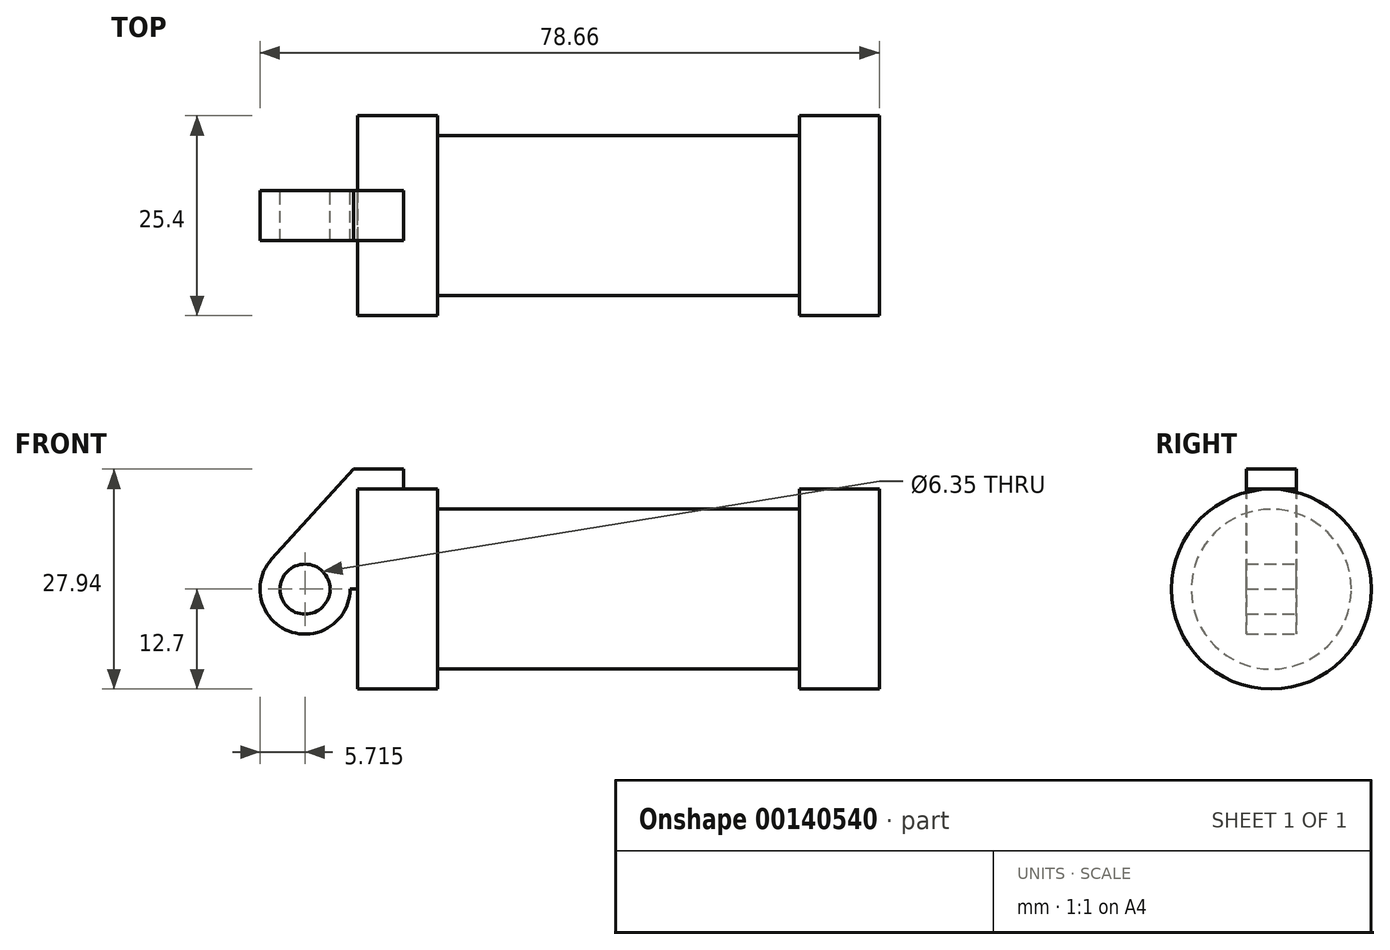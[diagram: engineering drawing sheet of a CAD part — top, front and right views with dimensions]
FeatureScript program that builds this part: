
annotation { "Feature Type Name" : "Feature", "Feature Type Description" : "" }
export const myFeature = defineFeature(function(context is Context, id is Id, definition is map)
    precondition{}
    {
        {
            var Q0;
            Q0=qCreatedBy(makeId("Front.planeOp"),FACE);
            var sketch = newSketch(context, id + "F0", { "sketchPlane" : qUnion([Q0])});
            skLineSegment(sketch, "E0", {"start": v(0, 0) * mm, "end": v(0, 12.7) * mm});
            skLineSegment(sketch, "E1", {"start": v(0, 12.7) * mm, "end": v(10.16, 12.7) * mm});
            skLineSegment(sketch, "E2", {"start": v(10.16, 12.7) * mm, "end": v(10.16, 10.16) * mm});
            skLineSegment(sketch, "E3", {"start": v(10.16, 10.16) * mm, "end": v(56.13, 10.16) * mm});
            skLineSegment(sketch, "E4", {"start": v(56.13, 10.16) * mm, "end": v(56.13, 12.7) * mm});
            skLineSegment(sketch, "E5", {"start": v(56.13, 12.7) * mm, "end": v(66.3, 12.7) * mm});
            skLineSegment(sketch, "E6", {"start": v(66.3, 12.7) * mm, "end": v(66.3, 0) * mm});
            skLineSegment(sketch, "E7", {"start": v(66.3, 0) * mm, "end": v(0, 0) * mm});
            skLineSegment(sketch, "E8", {"start": v(5.84, 15.24) * mm, "end": v(-0.5, 15.24) * mm});
            skLineSegment(sketch, "E9", {"start": v(-0.5, 15.24) * mm, "end": v(-10.88, 3.85) * mm});
            skLineSegment(sketch, "E10", {"start": v(0, 0) * mm, "end": v(-6.65, 0) * mm});
            skCircle(sketch, "E11", {"center": v(-6.65, 0) * mm, "radius": 5.72 * mm});
            skCircle(sketch, "E12", {"center": v(-6.65, 0) * mm, "radius": 3.18 * mm});
            skLineSegment(sketch, "E13", {"start": v(5.84, 15.24) * mm, "end": v(5.84, -9.4) * mm});
            skLineSegment(sketch, "E14", {"start": v(5.84, -9.4) * mm, "end": v(-8.18, -5.5) * mm});
            skSolve(sketch);
        }
        {
            var Q0;
            {var subQ0=sQuery(id+"F0.wireOp",EDGE,"E0");Q0=makeQuery(id+"F0.imprint","IMPRINT",FACE,{"disambiguationData":[TD([[makeQuery(id+"F0.imprint","IMPRINT",EDGE,{"derivedFrom":subQ0}),-1.0]])]});}
            var Q1;
            {var subQ0=sQuery(id+"F0.wireOp",EDGE,"E2");Q1=makeQuery(id+"F0.imprint","IMPRINT",FACE,{"disambiguationData":[TD([[makeQuery(id+"F0.imprint","IMPRINT",EDGE,{"derivedFrom":subQ0}),-1.0]])]});}
            var Q2;
            Q2=sQuery(id+"F0.wireOp",EDGE,"E7");
            revolve(context, id + "F1", {"entities" : qUnion([Q0, Q1]), "axis" : qUnion([Q2]), "revolveType" : RevolveType.FULL});
        }
        {
            var Q0;
            {var subQ4=sQuery(id+"F0.wireOp",EDGE,"E12");Q0=makeQuery(id+"F0.imprint","IMPRINT",FACE,{"disambiguationData":[TD([[makeQuery(id+"F0.imprint","IMPRINT",EDGE,{"derivedFrom":subQ4}),-1.0]])]});}
            var Q1;
            {var subQ3=sQuery(id+"F0.wireOp",EDGE,"E0");Q1=makeQuery(id+"F0.imprint","IMPRINT",FACE,{"disambiguationData":[TD([[makeQuery(id+"F0.imprint","IMPRINT",EDGE,{"derivedFrom":subQ3}),1.0]])]});}
            extrude(context, id + "F2", {"entities" : qUnion([Q0, Q1]), "endBound" : BoundingType.SYMMETRIC, "depth" : 6.35 * mm});
        }
    });
